# Revit family: 11
name_source: partatom
category: Plumbing Fixtures
units: mm (PartAtom-declared; Revit-internal decimal feet)

## family parameters
Cut with Voids When Loaded = No
Host = Face
OmniClass Number = 23.45.05.21.11.11
OmniClass Title = Water Operated Water Closets
Part Type = Normal
Room Calculation Point = No
Round Connector Dimension = Use Radius
Shared = Yes

## types (1)
- 2257528.020
    5901.100 - Heavy duty open front less cover = No
    5905.100 - Extra heavy duty open front less cover = No
    6065.121 - Ultima™ Selectronic Touchless Toilet Flush Valve = Yes
    ADA Compliant = Yes
    Assembly Code = D2010110
    Bowl Shape = Elongated
    CW Connection = Yes
    CWFU = 5
    Cold Water Connection Diameter = 1"
    Cold Water Connection Radius = 1/2"
    Cold Water Connection Width = 4 1/4"
    Cold Water Connection Width Constraint = 4 1/4"
    Default Elevation = 15"
    Description = Afwall® Millennium® Wall-Hung Toilet System With Touchless Selectronic® Piston Flush Valve, 1.28 gpf/4.8 Lpf
    EPA WaterSense® Certified = Yes
    Finish = Vitreous China-American Standard-020-White
    Flow Rate = 25gpm (94.6 L/min.)
    Flush Rate = 1.1 gpf to 1.6 gpf (4.2 Lpf to 6.0 Lpf)
    HW Connection = No
    HWFU = 0
    IAPMO Compliance = Meets or Exceeds the Following Specifications: ASME A112.19.2-2008 / CSA B45.1-08 for Vitreous China Fixtures
    Inlet Spud Size = 2"
    Installation Type = Floor Mounted
    Manufacturer = American Standard
    Material = Vitreous China-American Standard-020-White
    Model = 2257528.020
    Nominal Height = 13"
    Nominal Length = 26"
    Nominal Width = 14"
    Operating Pressure = 25 psi (flowing) - 80 psi (static)
    Power Supply = Factory-Installed CR-P2 Lithium Battery
    Product Documentation Link = https://americanstandard.box.com
    Product Page URL = https://www.americanstandard-us.com
    Spud Radius = 3/4"
    Supply Horizontal Offset = 4 3/4"
    Supply Verticall Offset = 11 1/2"
    URL = http://www.americanstandard-us.com
    Vent Connection = Yes
    WFU = 5
    Warranty Information = 5-YEAR LIMITED WARRANTY on FIXTURE and FLUSH VALVE
    Waste Connection = Yes
    Waste Connection Diameter = 4"
    Waste Connection Radius = 2"

## geometry (parser evidence)
native form markers: Sweep x4
no freeform markers — native parametric forms only
